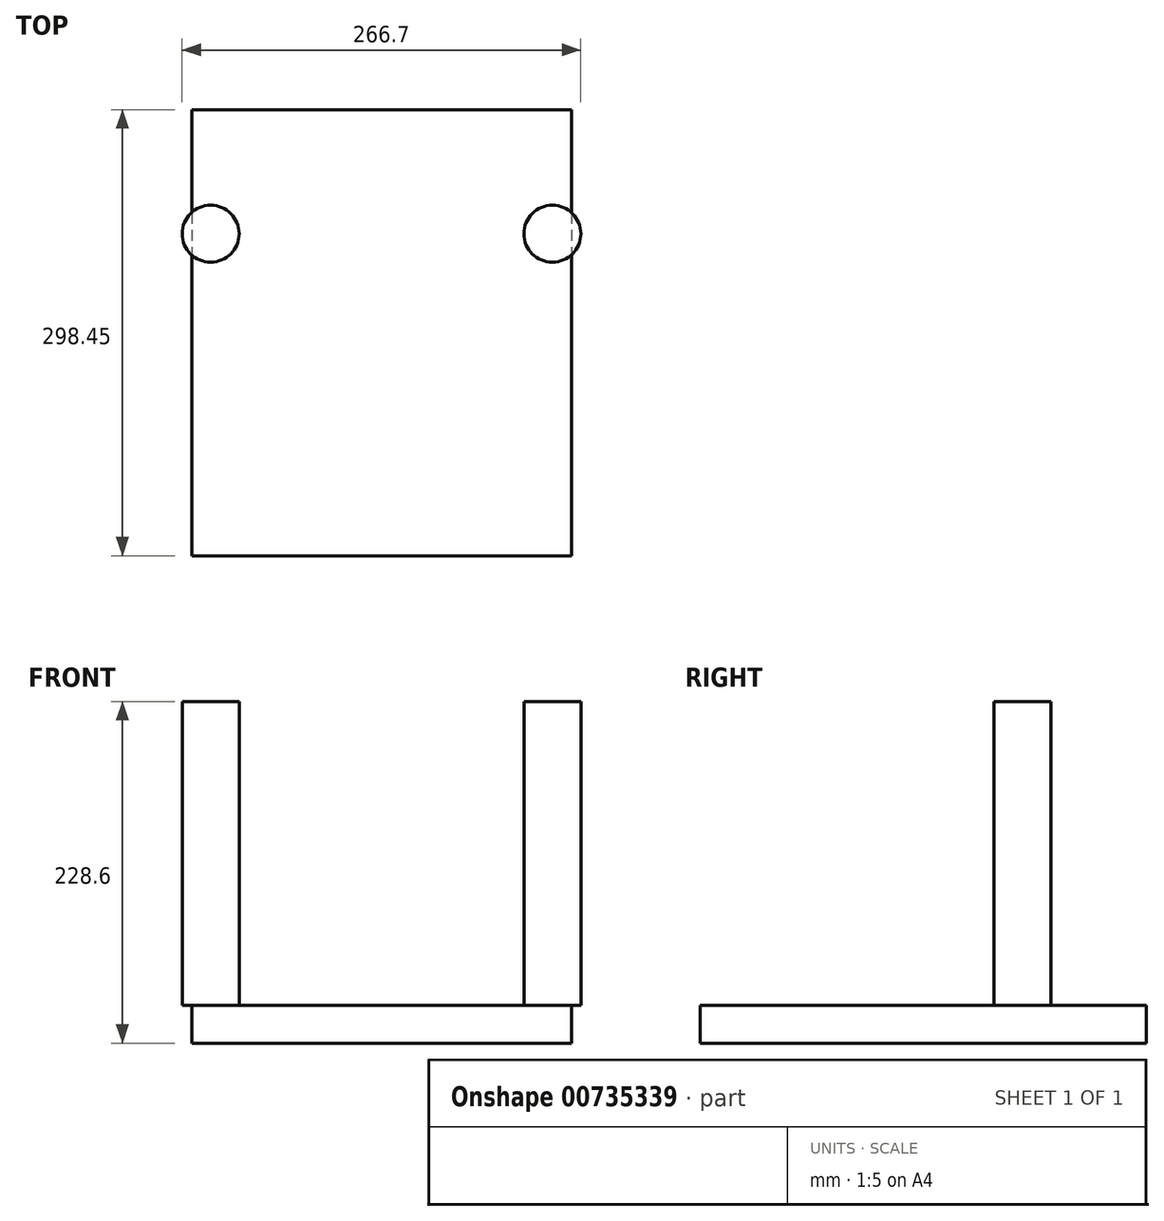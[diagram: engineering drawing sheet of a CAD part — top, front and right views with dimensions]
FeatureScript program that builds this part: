
annotation { "Feature Type Name" : "Feature", "Feature Type Description" : "" }
export const myFeature = defineFeature(function(context is Context, id is Id, definition is map)
    precondition{}
    {
        {
            var Q0;
            Q0=qCreatedBy(makeId("Top.planeOp"),FACE);
            var sketch = newSketch(context, id + "F0", { "sketchPlane" : qUnion([Q0])});
            skLineSegment(sketch, "E0", {"start": v(-59.36, 24.27) * mm, "end": v(143.84, 24.27) * mm});
            skCircle(sketch, "E1", {"center": v(156.54, 11.57) * mm, "radius": 19.05 * mm});
            skPoint(sketch, "E1.centerSnap0", {"position": v(169.24, 11.57) * mm});
            skPoint(sketch, "E1.centerSnap1", {"position": v(156.54, 24.27) * mm});
            skCircle(sketch, "E2", {"center": v(-72.06, 11.57) * mm, "radius": 19.05 * mm});
            skPoint(sketch, "E2.centerSnap0", {"position": v(-59.36, 11.57) * mm});
            skPoint(sketch, "E2.centerSnap1", {"position": v(-72.06, 24.27) * mm});
            skSolve(sketch);
        }
        {
            var Q0;
            Q0 = qSketchRegion(id + "F0", true);
            extrude(context, id + "F1", {"entities" : qUnion([Q0]), "depth" : 203.2 * mm, "offsetDistance" : 25.4 * mm});
        }
        {
            var Q0;
            Q0=qCreatedBy(makeId("Top.planeOp"),FACE);
            var sketch = newSketch(context, id + "F2", { "sketchPlane" : qUnion([Q0])});
            skLineSegment(sketch, "E3.left", {"start": v(169.29, 18.45) * mm, "end": v(169.29, -203.8) * mm});
            skLineSegment(sketch, "E3.right", {"start": v(-84.71, 18.45) * mm, "end": v(-84.71, -210.15) * mm});
            skLineSegment(sketch, "E4", {"start": v(-84.71, -203.8) * mm, "end": v(169.29, -203.8) * mm});
            skCircle(sketch, "E5", {"center": v(42.29, 0) * mm, "radius": 3.95 * mm});
            skLineSegment(sketch, "E6", {"start": v(-84.71, 18.45) * mm, "end": v(-84.71, 94.65) * mm});
            skLineSegment(sketch, "E7", {"start": v(169.29, 94.65) * mm, "end": v(169.29, 18.45) * mm});
            skLineSegment(sketch, "E8", {"start": v(-84.71, 94.65) * mm, "end": v(37.2, 94.65) * mm});
            skLineSegment(sketch, "E9", {"start": v(37.2, 94.65) * mm, "end": v(169.29, 94.65) * mm});
            skSolve(sketch);
        }
        {
            var Q0;
            Q0=makeQuery(id+"F2.imprint","IMPRINT",FACE,{"disambiguationData":[TD([[makeQuery(id+"F2.imprint","IMPRINT",EDGE,{"derivedFrom":sQuery(id+"F2.wireOp",EDGE,"E5")}),1.0]])]});
            var Q1;
            Q1=makeQuery(id+"F2.imprint","IMPRINT",FACE,{"disambiguationData":[TD([[makeQuery(id+"F2.imprint","IMPRINT",EDGE,{"derivedFrom":sQuery(id+"F2.wireOp",EDGE,"E3.left")}),-1.0]])]});
            extrude(context, id + "F3", {"entities" : qUnion([Q0, Q1]), "oppositeDirection" : true, "depth" : 25.4 * mm, "offsetDistance" : 25.4 * mm});
        }
        {
            var Q0;
            Q0=qCreatedBy(makeId("Top.planeOp"),FACE);
            var Q1;
            Q1=qCreatedBy(makeId("Front.planeOp"),FACE);
            cPlane(context, id + "F4", {"entities" : qUnion([Q0, Q1]), "cplaneType" : CPlaneType.MID_PLANE, "offset" : 25.4 * mm, "width" : 152.4 * mm, "height" : 152.4 * mm});
        }
        {
            var Q0;
            Q0=qCreatedBy(id+"F4.planeOp",FACE);
            var Q1;
            Q1=qCreatedBy(makeId("Top.planeOp"),FACE);
            cPlane(context, id + "F5", {"entities" : qUnion([Q0, Q1]), "cplaneType" : CPlaneType.MID_PLANE, "offset" : 25.4 * mm, "oppositeDirection" : true, "width" : 152.4 * mm, "height" : 152.4 * mm});
        }
        {
            var Q0;
            Q0=qCreatedBy(id+"F5.planeOp",FACE);
            var sketch = newSketch(context, id + "F6", { "sketchPlane" : qUnion([Q0])});
            skCircle(sketch, "E10", {"center": v(-24.9, -13.31) * mm, "radius": 6.35 * mm});
            skCircle(sketch, "E11", {"center": v(74.07, -13.31) * mm, "radius": 6.35 * mm});
            skSolve(sketch);
        }
        {
            var Q0;
            Q0=sQuery(id+"F6.wireOp",EDGE,"E10");
            var Q1;
            Q1=sQuery(id+"F6.wireOp",EDGE,"E11");
            extrude(context, id + "F7", {"bodyType" : ToolBodyType.SURFACE, "surfaceEntities" : qUnion([Q0, Q1]), "depth" : 177.8 * mm, "offsetDistance" : 25.4 * mm});
        }
        {
            var Q0;
            Q0=makeQuery(id+"F7.opExtrude","SWEPT_BODY",BODY,{"disambiguationData":[OSD([sQuery(id+"F6.wireOp",EDGE,"E11")])]});
            var Q1;
            Q1=makeQuery(id+"F7.opExtrude","SWEPT_BODY",BODY,{"disambiguationData":[OSD([sQuery(id+"F6.wireOp",EDGE,"E10")])]});
            transform(context, id + "F8", {"entities" : qUnion([Q0, Q1]), "transformType" : TransformType.TRANSLATION_3D, "dx" : 0 * mm, "dy" : -120.4 * mm, "dz" : 65.8 * mm, "makeCopy" : false});
        }
        {
            var Q0;
            Q0=sQuery(id+"F2.wireOp",EDGE,"E5");
            extrude(context, id + "F9", {"bodyType" : ToolBodyType.SURFACE, "surfaceEntities" : qUnion([Q0]), "depth" : 25.4 * mm, "offsetDistance" : 25.4 * mm});
        }
    });
